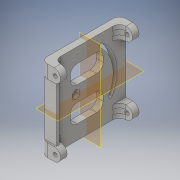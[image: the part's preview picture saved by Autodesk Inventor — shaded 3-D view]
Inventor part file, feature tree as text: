
AUTODESK INVENTOR PART (.ipt)
format: ipt  version: 2016 (Build 200138000, 138)  size: 352,256 bytes
history: native  units: in
note: dims shown in document units (in); Inventor stores cm internally (conversion verified against a paired STEP export)
features: plane x2, mirror x2, other x1, extrude x1, sketch x1, projected_geometry x1
ambient origin geometry x8: Origin, YZ Plane, XZ Plane, XY Plane, X Axis, Y Axis, Z Axis, Center Point
bodies: Solid1 (feature_tree)
feature tree (8):
  other  "Pen Carriage"
  plane  "Work Plane1"
  plane  "Work Plane2"
  extrude  "Extrusion1"  Depth=0.1969in
  mirror  "Mirror1"
  mirror  "Mirror2"
  sketch  "Sketch1"  dims[d0=0.1173in d1=0.1969in d2=0.3937in d3=0.0in]
  projected_geometry  "Projected Loop1"
